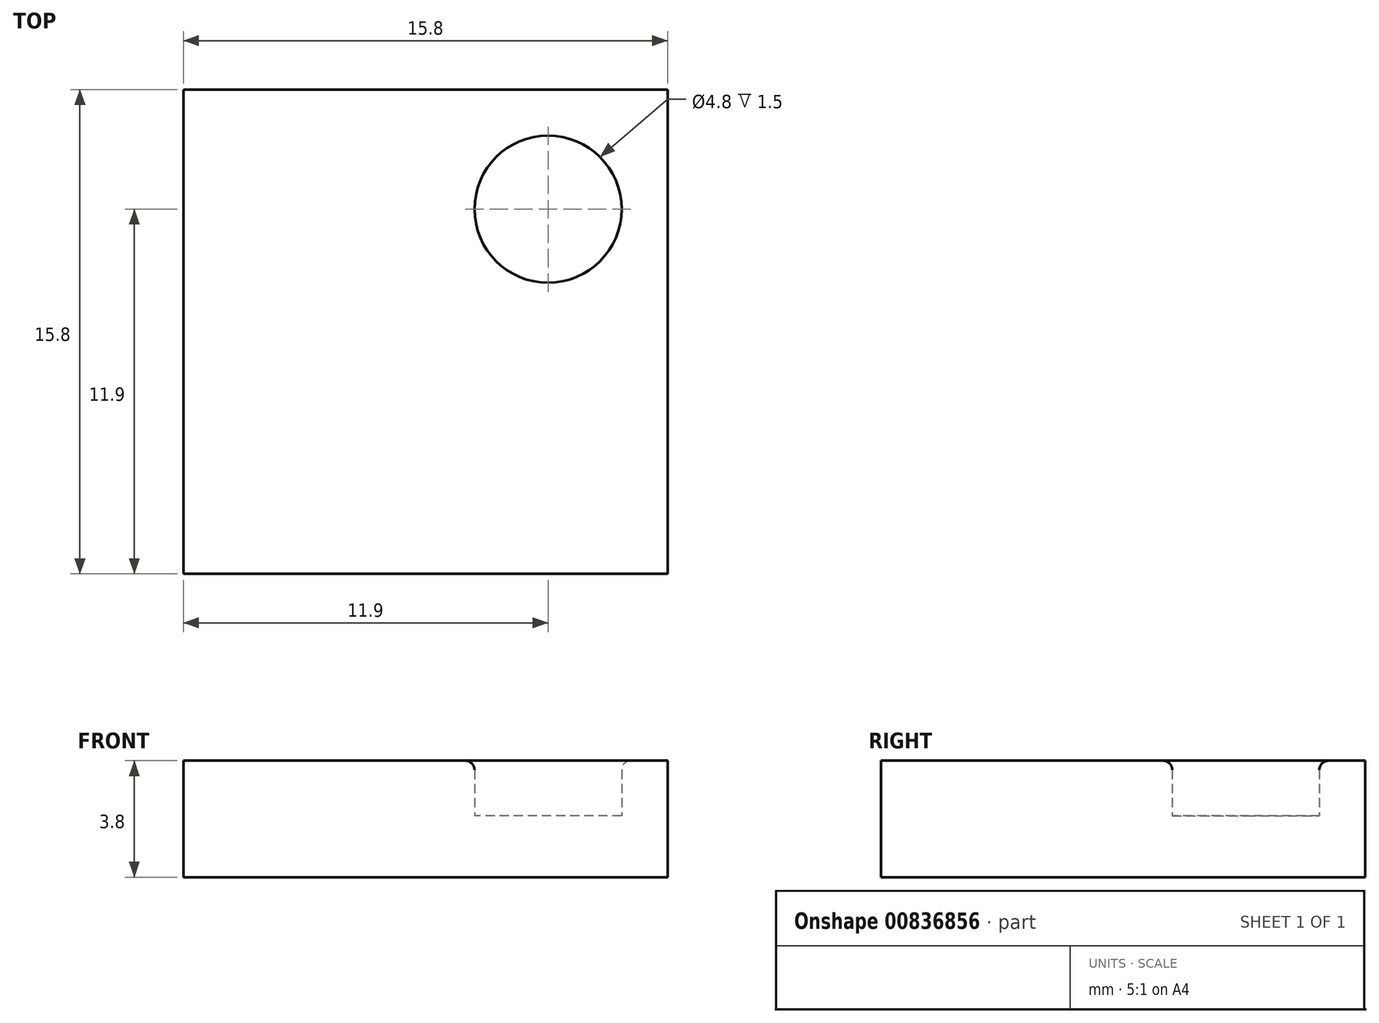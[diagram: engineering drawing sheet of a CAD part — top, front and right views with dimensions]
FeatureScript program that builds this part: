
annotation { "Feature Type Name" : "Feature", "Feature Type Description" : "" }
export const myFeature = defineFeature(function(context is Context, id is Id, definition is map)
    precondition{}
    {
        {
            var Q0;
            Q0=qCreatedBy(makeId("Top.planeOp"),FACE);
            var sketch = newSketch(context, id + "F0", { "sketchPlane" : qUnion([Q0])});
            skLineSegment(sketch, "E0.bottom", {"start": v(7.9, -7.9) * mm, "end": v(-7.9, -7.9) * mm});
            skLineSegment(sketch, "E0.top", {"start": v(7.9, 7.9) * mm, "end": v(-7.9, 7.9) * mm});
            skLineSegment(sketch, "E0.left", {"start": v(7.9, -7.9) * mm, "end": v(7.9, 7.9) * mm});
            skLineSegment(sketch, "E0.right", {"start": v(-7.9, -7.9) * mm, "end": v(-7.9, 7.9) * mm});
            skPoint(sketch, "E0.middle", {"position": v(0, 0) * mm});
            skSolve(sketch);
        }
        {
            var Q0;
            Q0=makeQuery(id+"F0.imprint","IMPRINT",FACE,{"disambiguationData":[TD([[makeQuery(id+"F0.imprint","IMPRINT",EDGE,{"derivedFrom":sQuery(id+"F0.wireOp",EDGE,"E0.bottom")}),-1.0]])]});
            extrude(context, id + "F1", {"entities" : qUnion([Q0]), "depth" : 2 * mm, "offsetDistance" : 25 * mm});
        }
        {
            var Q0;
            Q0=makeQuery(id+"F1.opExtrude","CAP_FACE",FACE,{"disambiguationData":[OSD([sQuery(id+"F0.wireOp",EDGE,"E0.bottom"),sQuery(id+"F0.wireOp",EDGE,"E0.top"),sQuery(id+"F0.wireOp",EDGE,"E0.left"),sQuery(id+"F0.wireOp",EDGE,"E0.right")])],"isStart":false});
            var sketch = newSketch(context, id + "F2", { "sketchPlane" : qUnion([Q0])});
            skCircle(sketch, "E1", {"center": v(-4, 4) * mm, "radius": 2.4 * mm});
            skCircle(sketch, "E2.MirrorC", {"center": v(4, 4) * mm, "radius": 2.4 * mm});
            skSolve(sketch);
        }
        {
            var Q0;
            Q0=makeQuery(id+"F2.imprint","IMPRINT",FACE,{"disambiguationData":[TD([[makeQuery(id+"F2.imprint","IMPRINT",EDGE,{"derivedFrom":sQuery(id+"F2.wireOp",EDGE,"E1")}),1.0]])]});
            var Q1;
            Q1=makeQuery(id+"F2.imprint","IMPRINT",FACE,{"disambiguationData":[TD([[makeQuery(id+"F2.imprint","IMPRINT",EDGE,{"derivedFrom":sQuery(id+"F2.wireOp",EDGE,"E2.MirrorC")}),-1.0]])]});
            extrude(context, id + "F3", {"entities" : qUnion([Q0, Q1]), "operationType" : NewBodyOperationType.ADD, "depth" : 1.8 * mm, "offsetDistance" : 25 * mm});
        }
        {
            var Q0;
            Q0=makeQuery(id+"F3.opExtrude","CAP_EDGE",EDGE,{"disambiguationData":[OSD([sQuery(id+"F2.wireOp",EDGE,"E2.MirrorC")])],"isStart":false});
            var Q1;
            Q1=makeQuery(id+"F3.opExtrude","CAP_EDGE",EDGE,{"disambiguationData":[OSD([sQuery(id+"F2.wireOp",EDGE,"E1")])],"isStart":false});
            fillet(context, id + "F4", {"entities" : qUnion([Q0, Q1]), "radius" : 0.3 * mm, "tangentPropagation" : true, "allowEdgeOverflow" : false});
        }
    });
